# Revit family: 33902-presto
name_source: partatom
category: Plumbing Fixtures
units: mm (PartAtom-declared; Revit-internal decimal feet)

## family parameters
Always vertical = Yes
Cut with Voids When Loaded = No
Maintain Annotation Orientation = No
Part Type = Normal
Room Calculation Point = No
Round Connector Dimension = Use Diameter
Shared = No
Work Plane-Based = Yes

## types (1)
- 33902- Les Robinets PRESTO
    - Hydraulic supply = 15.00 mm
    -Delivered with = 2 coloured marker (Red and blue) Instruction manual
    > Standards & approvals = Acoustic class II
Brass body in accordance with EN 1982, EN 12164, EN 12165
Molded chrome-plated body in accordance with EN 12540
200-hour neutral salt spray resistant (NSS) in accordance with ISO 9227
    > Thermal resistance : = 75.0000 (m²·K)/W
    Default Elevation = 1219 mm
    Description = Single wall-mounted tap
    Model = 33902
    Recommended pressure = 3.0 bar
    Type Comments = wall mounted tap
    URL = https://www.prestodatashare.com
    brand = Les Robinets PRESTO
    flow = 3.0 L/min
    material = Stainless Steel AISI 304
    material 2 = Default
    min pressure = 1.0 bar
    pressure = 5.0 bar
    range = Single wall-mounted tap
    ref = 33902 - PRESTO 504 S, anti-blocking "S" system, antifreeze

## geometry (parser evidence)
native form markers: Sweep x8
no freeform markers — native parametric forms only
